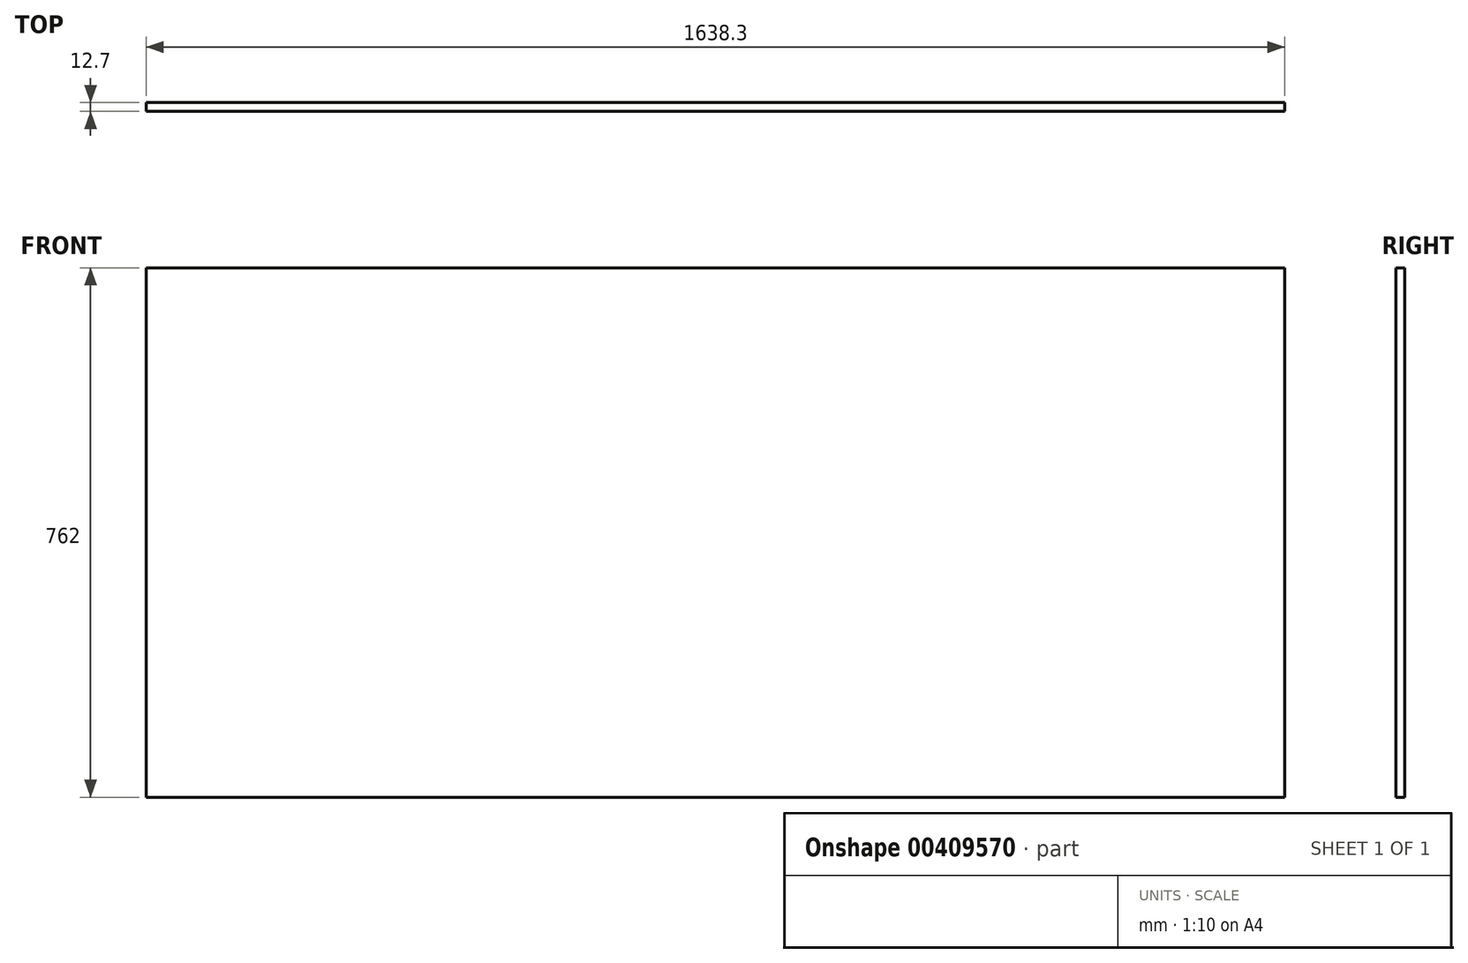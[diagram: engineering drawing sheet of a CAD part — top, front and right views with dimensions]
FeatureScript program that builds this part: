
annotation { "Feature Type Name" : "Feature", "Feature Type Description" : "" }
export const myFeature = defineFeature(function(context is Context, id is Id, definition is map)
    precondition{}
    {
        {
            var Q0;
            Q0=qCreatedBy(makeId("Front.planeOp"),FACE);
            var sketch = newSketch(context, id + "F0", { "sketchPlane" : qUnion([Q0])});
            skLineSegment(sketch, "E0.bottom", {"start": v(-818.24, 308.69) * mm, "end": v(820.06, 308.69) * mm});
            skLineSegment(sketch, "E0.top", {"start": v(-818.24, -453.31) * mm, "end": v(820.06, -453.31) * mm});
            skLineSegment(sketch, "E0.left", {"start": v(-818.24, 308.69) * mm, "end": v(-818.24, -453.31) * mm});
            skLineSegment(sketch, "E0.right", {"start": v(820.06, 308.69) * mm, "end": v(820.06, -453.31) * mm});
            skSolve(sketch);
        }
        {
            var Q0;
            Q0=makeQuery(id+"F0.imprint","IMPRINT",FACE,{"disambiguationData":[TD([[makeQuery(id+"F0.imprint","IMPRINT",EDGE,{"derivedFrom":sQuery(id+"F0.wireOp",EDGE,"E0.bottom")}),-1.0]])]});
            extrude(context, id + "F1", {"entities" : qUnion([Q0]), "depth" : 12.7 * mm});
        }
    });
